# Revit family: Auto
name_source: partatom
category: Mechanical Equipment
units: mm (PartAtom-declared; Revit-internal decimal feet)

## family parameters
Always vertical = Yes
Classification = None
Cut with Voids When Loaded = No
Part Type = Normal
Room Calculation Point = No
Round Connector Dimension = Use Diameter
Shared = No
Work Plane-Based = No

## types (3) — shared parameters
00_20_Manufacturer = Blauberg
00_20_Name = 'Extraction fan
Amperage = 0 A
Casing Material = Plastic, opaque, white
Description = For round channels
Frequency = 50 Hz
Load Classification = HVAC
Maintenance zone material = <By Category>
Manufacturer = Blauberg
Number of Fase = 1
URL = https://blaubergventilatoren.de
Voltage = 230 V
Панель = panel
zero-valued in all types: Default Elevation

## per-type parameters (varying)
| type | Apparent Load | Diameter | Dy | H | Height | L2 | Length | Maximum Air Flow | Power | Sound pressure level at 3 m distance | Weight | Width | a | c | d | e |
| Auto 150 | 30 W | 150 mm | 145 mm  [stored 0.475722 ft] | 210 mm  [stored 0.688976 ft] | 210 mm  [stored 0.688976 ft] | 81 mm  [stored 0.265748 ft] | 149 mm  [stored 0.488845 ft] | 295.0 m³/h | 26 W | 39 dBA | 1.02 kg | 210 mm  [stored 0.688976 ft] | 210 mm  [stored 0.688976 ft] | 115 mm  [stored 0.377297 ft] | 150 mm | 34 mm |
| Auto 125 | 23 W | 125 mm  [stored 0.410105 ft] | 120 mm  [stored 0.393701 ft] | 186 mm  [stored 0.610236 ft] | 186 mm  [stored 0.610236 ft] | 65 mm  [stored 0.213255 ft] | 131 mm  [stored 0.42979 ft] | 185.0 m³/h | 22 W | 35 dBA | 0.75 kg | 186 mm  [stored 0.610236 ft] | 186 mm  [stored 0.610236 ft] | 98 mm  [stored 0.321522 ft] | 125 mm  [stored 0.410105 ft] | 33 mm  [stored 0.108268 ft] |
| Auto 100 | 21 W | 100 mm  [stored 0.328084 ft] | 95 mm | 166 mm  [stored 0.544619 ft] | 166 mm  [stored 0.544619 ft] | 60 mm  [stored 0.19685 ft] | 120 mm  [stored 0.393701 ft] | 98.0 m³/h | 18 W | 34 dBA | 0.65 kg | 166 mm  [stored 0.544619 ft] | 166 mm  [stored 0.544619 ft] | 90 mm  [stored 0.295276 ft] | 100 mm  [stored 0.328084 ft] | 30 mm  [stored 0.0984252 ft] |

note: column(s) folded — value = type name in every type: 00_20_Type

note: [stored X ft] marks values corroborated as IEEE doubles in the binary element streams (Revit-internal decimal feet)
